# Revit family: Coifa Incasso 75
name_source: partatom
category: Modelos genéricos
units: mm (PartAtom-declared; Revit-internal decimal feet)

## family parameters
Compartilhado = Sim
Corte com vazios quando carregada = Não
Cota do conector redondo = Utilizar diâmetro
Pode hospedar o vergalhão = Não
Ponto de cálculo do ambiente = Não
Sempre na vertical = Não
Tipo de parte = Não definido

## types (1)
- Coifa Incasso 75
    Acabamento = Black Steel
    Acessório opcional = Tampa externa em aço Inox
    Acessórios inclusos = 1 Duto de Alumínio, 1 Defletor, 2 Filtros de Carvão Ativado
    Descrição = Coifa de Embutir
    Elevação padrão = 0 mm  [stored 0 ft]
    Fabricante = Tramontina
    Frequência = 50-60 Hz
    Material predominante = Aço Inox
    Modelo = Coifa de Embutir Incasso 75
    Nível de ruído emitido = 63 dB(A)
    Potência das lâmpadas = LED: 2x1,5 W
    Potência total = 260 W
    Quantidade de filtros = 2
    Quantidade de velocidades = 3
    Referência do produto = 95800/016
    Tensão de operação = 220 V
    URL da ficha técnica = https://assets.tramontina.com.br
    URL do fabricante = tramontina.com.br
    URL do produto = https://www.tramontina.com.br
    URL dos arquivos BIM = tramontina.com/biblioteca
    Vazão volumétrica = 630 m³/h

note: [stored X ft] marks values corroborated as IEEE doubles in the binary element streams (Revit-internal decimal feet)
